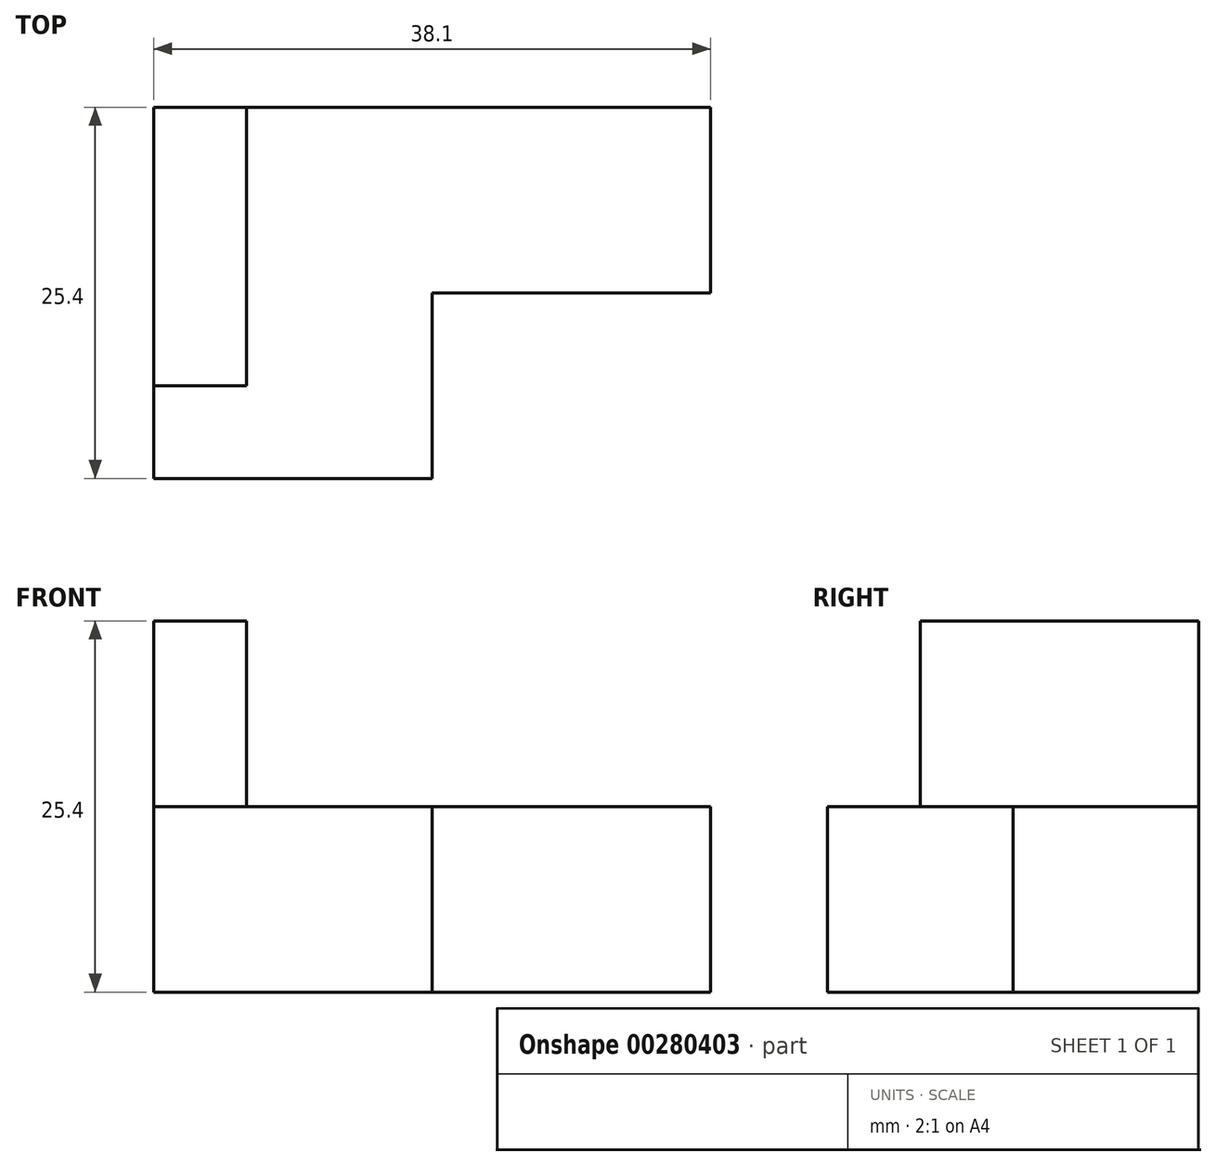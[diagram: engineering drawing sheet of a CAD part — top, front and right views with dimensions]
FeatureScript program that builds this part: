
annotation { "Feature Type Name" : "Feature", "Feature Type Description" : "" }
export const myFeature = defineFeature(function(context is Context, id is Id, definition is map)
    precondition{}
    {
        {
            var Q0;
            Q0=qCreatedBy(makeId("Front.planeOp"),FACE);
            var sketch = newSketch(context, id + "F0", { "sketchPlane" : qUnion([Q0])});
            skLineSegment(sketch, "E0", {"start": v(0, 0) * mm, "end": v(0, 25.4) * mm});
            skLineSegment(sketch, "E1", {"start": v(0, 25.4) * mm, "end": v(6.35, 25.4) * mm});
            skLineSegment(sketch, "E2", {"start": v(6.35, 25.4) * mm, "end": v(6.35, 12.7) * mm});
            skLineSegment(sketch, "E3", {"start": v(6.35, 12.7) * mm, "end": v(38.1, 12.7) * mm});
            skLineSegment(sketch, "E4", {"start": v(38.1, 12.7) * mm, "end": v(38.1, 0) * mm});
            skLineSegment(sketch, "E5", {"start": v(38.1, 0) * mm, "end": v(0, 0) * mm});
            skSolve(sketch);
        }
        {
            var Q0;
            Q0 = qSketchRegion(id + "F0", true);
            extrude(context, id + "F1", {"entities" : qUnion([Q0]), "depth" : 25.4 * mm});
        }
        {
            var Q0;
            Q0=makeQuery(id+"F1.opExtrude","SWEPT_FACE",FACE,{"disambiguationData":[OSD([sQuery(id+"F0.wireOp",EDGE,"E2")])]});
            var sketch = newSketch(context, id + "F2", { "sketchPlane" : qUnion([Q0])});
            skLineSegment(sketch, "E6", {"start": v(-25.4, 25.4) * mm, "end": v(-19.05, 25.4) * mm});
            skLineSegment(sketch, "E7", {"start": v(-19.05, 25.4) * mm, "end": v(-19.05, 12.7) * mm});
            skLineSegment(sketch, "E8", {"start": v(-19.05, 12.7) * mm, "end": v(-25.4, 12.7) * mm});
            skLineSegment(sketch, "E9", {"start": v(-25.4, 12.7) * mm, "end": v(-25.4, 25.4) * mm});
            skSolve(sketch);
        }
        {
            var Q0;
            Q0 = qSketchRegion(id + "F2", true);
            extrude(context, id + "F3", {"entities" : qUnion([Q0]), "operationType" : NewBodyOperationType.REMOVE, "oppositeDirection" : true, "depth" : 25.4 * mm});
        }
        {
            var Q0;
            Q0=makeQuery(id+"F3.boolean.opBoolean","MERGE",FACE,{"derivedFrom":[makeQuery(id+"F1.opExtrude","SWEPT_FACE",FACE,{"disambiguationData":[OSD([sQuery(id+"F0.wireOp",EDGE,"E3")])]}),makeQuery(id+"F3.opExtrude","SWEPT_FACE",FACE,{"disambiguationData":[OSD([sQuery(id+"F2.wireOp",EDGE,"E8")])]})]});
            var sketch = newSketch(context, id + "F4", { "sketchPlane" : qUnion([Q0])});
            skLineSegment(sketch, "E10", {"start": v(38.1, -25.4) * mm, "end": v(19.05, -25.4) * mm});
            skLineSegment(sketch, "E11", {"start": v(19.05, -25.4) * mm, "end": v(19.05, -12.7) * mm});
            skLineSegment(sketch, "E12", {"start": v(19.05, -12.7) * mm, "end": v(38.1, -12.7) * mm});
            skLineSegment(sketch, "E13", {"start": v(38.1, -12.7) * mm, "end": v(38.1, -25.4) * mm});
            skSolve(sketch);
        }
        {
            var Q0;
            Q0 = qSketchRegion(id + "F4", true);
            extrude(context, id + "F5", {"entities" : qUnion([Q0]), "operationType" : NewBodyOperationType.REMOVE, "oppositeDirection" : true, "depth" : 25.4 * mm});
        }
    });
